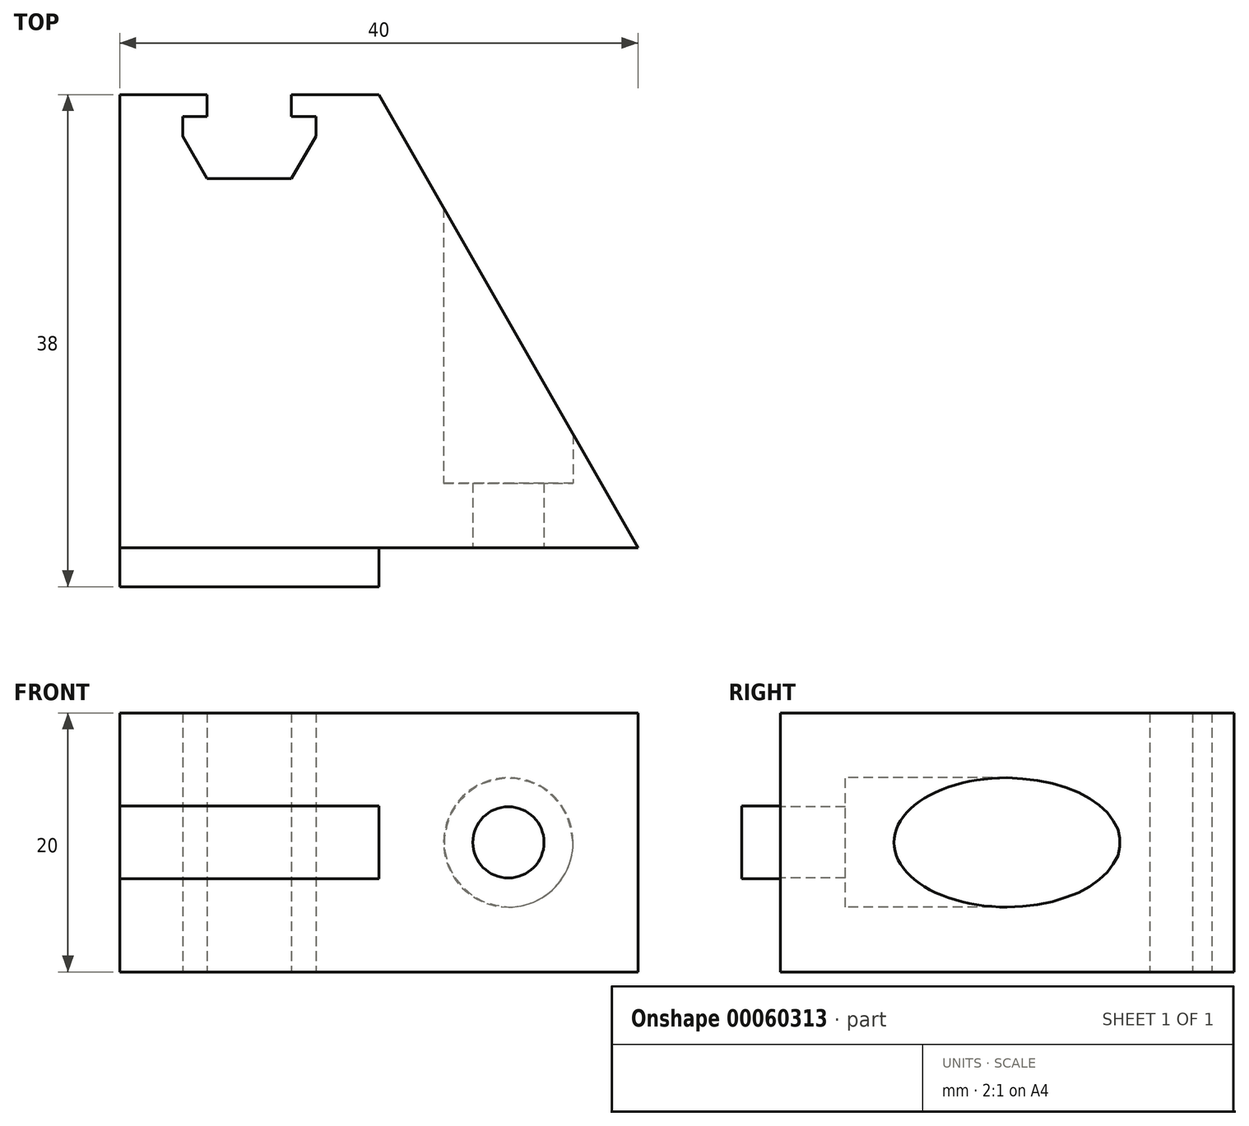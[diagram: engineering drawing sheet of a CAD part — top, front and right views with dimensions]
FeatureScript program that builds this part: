
annotation { "Feature Type Name" : "Feature", "Feature Type Description" : "" }
export const myFeature = defineFeature(function(context is Context, id is Id, definition is map)
    precondition{}
    {
        {
            var Q0;
            Q0=qCreatedBy(makeId("Top.planeOp"),FACE);
            var sketch = newSketch(context, id + "F0", { "sketchPlane" : qUnion([Q0])});
            skLineSegment(sketch, "E0.bottom", {"start": v(-10, 17.5) * mm, "end": v(-3.25, 17.5) * mm});
            skLineSegment(sketch, "E0.top", {"start": v(-10, -17.5) * mm, "end": v(10, -17.5) * mm});
            skLineSegment(sketch, "E0.left", {"start": v(-10, 17.5) * mm, "end": v(-10, -17.5) * mm});
            skLineSegment(sketch, "E0.right", {"start": v(10, 17.5) * mm, "end": v(10, -17.5) * mm});
            skLineSegment(sketch, "E1", {"start": v(-10, 0) * mm, "end": v(10, 0) * mm, "construction": true});
            skLineSegment(sketch, "E2", {"start": v(10, -17.5) * mm, "end": v(30, -17.5) * mm});
            skLineSegment(sketch, "E3", {"start": v(30, -17.5) * mm, "end": v(10, 17.5) * mm});
            skLineSegment(sketch, "E4", {"start": v(-3.25, 17.5) * mm, "end": v(-3.25, 15.8) * mm});
            skLineSegment(sketch, "E5", {"start": v(3.25, 15.8) * mm, "end": v(3.25, 17.5) * mm});
            skLineSegment(sketch, "E6", {"start": v(-3.25, 15.8) * mm, "end": v(-5.15, 15.8) * mm});
            skLineSegment(sketch, "E7", {"start": v(3.25, 15.8) * mm, "end": v(5.15, 15.8) * mm});
            skLineSegment(sketch, "E8", {"start": v(-3.25, 11) * mm, "end": v(3.25, 11) * mm});
            skLineSegment(sketch, "E9", {"start": v(-5.15, 15.8) * mm, "end": v(-5.15, 14.3) * mm});
            skLineSegment(sketch, "E10", {"start": v(5.15, 15.8) * mm, "end": v(5.15, 14.3) * mm});
            skLineSegment(sketch, "E11", {"start": v(-5.15, 14.3) * mm, "end": v(-3.25, 11) * mm});
            skLineSegment(sketch, "E12", {"start": v(5.15, 14.3) * mm, "end": v(3.25, 11) * mm});
            skLineSegment(sketch, "E13.trimOffspring", {"start": v(3.25, 17.5) * mm, "end": v(10, 17.5) * mm});
            skLineSegment(sketch, "E14", {"start": v(0, 0) * mm, "end": v(0, 11) * mm, "construction": true});
            skSolve(sketch);
        }
        {
            var Q0;
            Q0 = qSketchRegion(id + "F0", true);
            extrude(context, id + "F1", {"entities" : qUnion([Q0]), "depth" : 20 * mm});
        }
        {
            var Q0;
            Q0=makeQuery(id+"F1.opExtrude","SWEPT_FACE",FACE,{"disambiguationData":[OSD([sQuery(id+"F0.wireOp",EDGE,"E0.top"),sQuery(id+"F0.wireOp",EDGE,"E2")])]});
            var sketch = newSketch(context, id + "F2", { "sketchPlane" : qUnion([Q0])});
            skLineSegment(sketch, "E15.bottom", {"start": v(30, 20) * mm, "end": v(10, 20) * mm, "construction": true});
            skLineSegment(sketch, "E15.top", {"start": v(30, 0) * mm, "end": v(10, 0) * mm, "construction": true});
            skLineSegment(sketch, "E15.left", {"start": v(30, 20) * mm, "end": v(30, 0) * mm, "construction": true});
            skLineSegment(sketch, "E15.right", {"start": v(10, 20) * mm, "end": v(10, 0) * mm, "construction": true});
            skLineSegment(sketch, "E16", {"start": v(20, 20) * mm, "end": v(20, 0) * mm, "construction": true});
            skCircle(sketch, "E17", {"center": v(20, 10) * mm, "radius": 2.75 * mm});
            skCircle(sketch, "E18", {"center": v(20, 10) * mm, "radius": 5 * mm});
            skLineSegment(sketch, "E19", {"start": v(10, 10) * mm, "end": v(-10, 10) * mm, "construction": true});
            skLineSegment(sketch, "E20", {"start": v(10, 12.8) * mm, "end": v(-10, 12.8) * mm});
            skLineSegment(sketch, "E21", {"start": v(10, 7.2) * mm, "end": v(-10, 7.2) * mm});
            skLineSegment(sketch, "E22", {"start": v(-10, 12.8) * mm, "end": v(-10, 7.2) * mm});
            skLineSegment(sketch, "E23", {"start": v(10, 12.8) * mm, "end": v(10, 7.2) * mm});
            skSolve(sketch);
        }
        {
            var Q0;
            Q0=makeQuery(id+"F2.imprint","IMPRINT",FACE,{"disambiguationData":[TD([[makeQuery(id+"F2.imprint","IMPRINT",EDGE,{"derivedFrom":sQuery(id+"F2.wireOp",EDGE,"E17")}),1.0]])]});
            extrude(context, id + "F3", {"entities" : qUnion([Q0]), "operationType" : NewBodyOperationType.REMOVE, "oppositeDirection" : true, "depth" : 25 * mm});
        }
        {
            var Q0;
            Q0=makeQuery(id+"F2.imprint","IMPRINT",FACE,{"disambiguationData":[TD([[makeQuery(id+"F2.imprint","IMPRINT",EDGE,{"derivedFrom":sQuery(id+"F2.wireOp",EDGE,"E17")}),-1.0]])]});
            extrude(context, id + "F4", {"entities" : qUnion([Q0]), "operationType" : NewBodyOperationType.REMOVE, "oppositeDirection" : true, "depth" : 28.4 * mm});
        }
        {
            var Q0;
            Q0=makeQuery(id+"F2.imprint","IMPRINT",FACE,{"disambiguationData":[TD([[makeQuery(id+"F2.imprint","IMPRINT",EDGE,{"derivedFrom":sQuery(id+"F2.wireOp",EDGE,"E17")}),-1.0]])]});
            extrude(context, id + "F5", {"entities" : qUnion([Q0]), "operationType" : NewBodyOperationType.ADD, "oppositeDirection" : true, "depth" : 5 * mm});
        }
        {
            var Q0;
            Q0=makeQuery(id+"F2.imprint","IMPRINT",FACE,{"disambiguationData":[TD([[makeQuery(id+"F2.imprint","IMPRINT",EDGE,{"derivedFrom":sQuery(id+"F2.wireOp",EDGE,"E20")}),1.0]])]});
            extrude(context, id + "F6", {"entities" : qUnion([Q0]), "operationType" : NewBodyOperationType.ADD, "depth" : 3 * mm});
        }
    });
